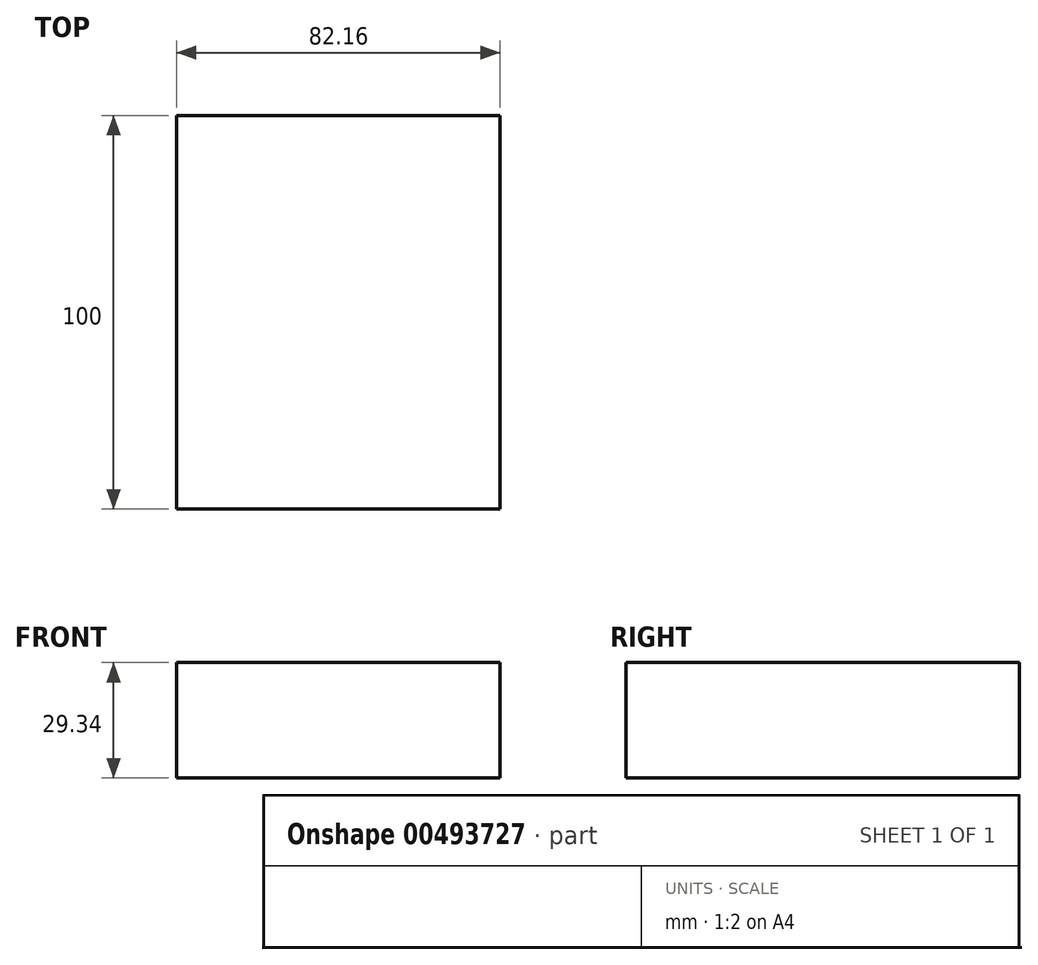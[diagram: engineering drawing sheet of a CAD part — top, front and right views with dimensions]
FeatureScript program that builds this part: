
annotation { "Feature Type Name" : "Feature", "Feature Type Description" : "" }
export const myFeature = defineFeature(function(context is Context, id is Id, definition is map)
    precondition{}
    {
        {
            var Q0;
            Q0=qCreatedBy(makeId("Front.planeOp"),FACE);
            var sketch = newSketch(context, id + "F0", { "sketchPlane" : qUnion([Q0])});
            skLineSegment(sketch, "E0.bottom", {"start": v(-41.08, 14.67) * mm, "end": v(41.08, 14.67) * mm});
            skLineSegment(sketch, "E0.top", {"start": v(-41.08, -14.67) * mm, "end": v(41.08, -14.67) * mm});
            skLineSegment(sketch, "E0.left", {"start": v(-41.08, 14.67) * mm, "end": v(-41.08, -14.67) * mm});
            skLineSegment(sketch, "E0.right", {"start": v(41.08, 14.67) * mm, "end": v(41.08, -14.67) * mm});
            skPoint(sketch, "E0.middle", {"position": v(0, 0) * mm});
            skSolve(sketch);
        }
        {
            var Q0;
            Q0=makeQuery(id+"F0.imprint","IMPRINT",FACE,{"disambiguationData":[TD([[makeQuery(id+"F0.imprint","IMPRINT",EDGE,{"derivedFrom":sQuery(id+"F0.wireOp",EDGE,"E0.bottom")}),-1.0]])]});
            extrude(context, id + "F1", {"entities" : qUnion([Q0]), "endBound" : BoundingType.SYMMETRIC, "depth" : 100 * mm});
        }
    });
